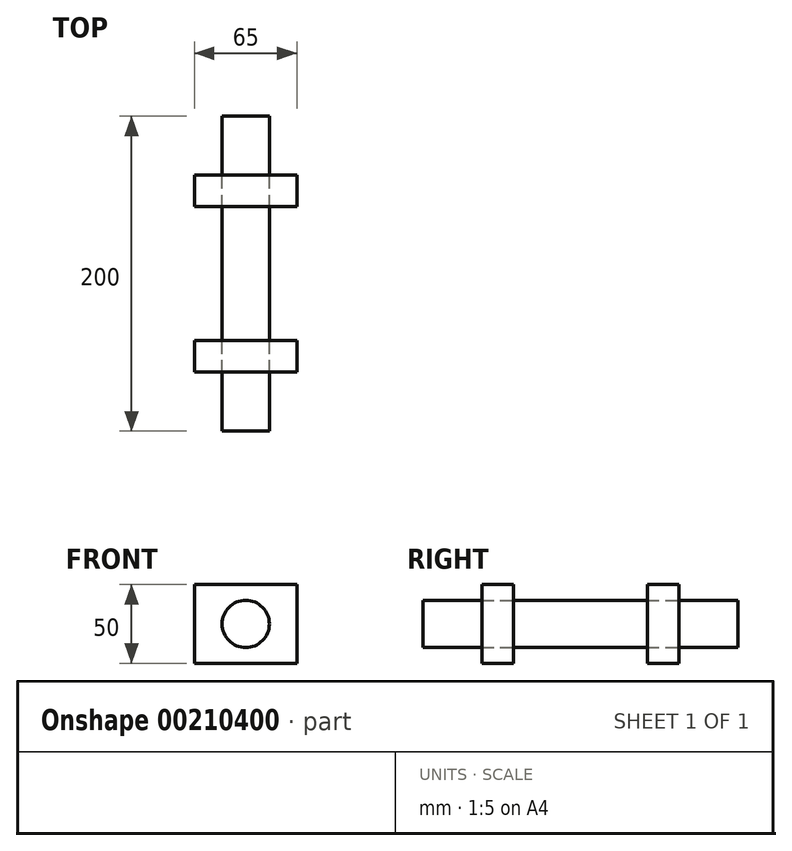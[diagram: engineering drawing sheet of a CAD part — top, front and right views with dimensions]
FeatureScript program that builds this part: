
annotation { "Feature Type Name" : "Feature", "Feature Type Description" : "" }
export const myFeature = defineFeature(function(context is Context, id is Id, definition is map)
    precondition{}
    {
        {
            var Q0;
            Q0=qCreatedBy(makeId("Front.planeOp"),FACE);
            var sketch = newSketch(context, id + "F0", { "sketchPlane" : qUnion([Q0])});
            skCircle(sketch, "E0", {"center": v(0, 0) * mm, "radius": 15 * mm});
            skSolve(sketch);
        }
        {
            var Q0;
            Q0=makeQuery(id+"F0.imprint","IMPRINT",FACE,{"disambiguationData":[TD([[makeQuery(id+"F0.imprint","IMPRINT",EDGE,{"derivedFrom":sQuery(id+"F0.wireOp",EDGE,"E0")}),1.0]])]});
            extrude(context, id + "F1", {"entities" : qUnion([Q0]), "endBound" : BoundingType.SYMMETRIC, "depth" : 200 * mm});
        }
        {
            var Q0;
            Q0=qCreatedBy(makeId("Top.planeOp"),FACE);
            var sketch = newSketch(context, id + "F2", { "sketchPlane" : qUnion([Q0])});
            skLineSegment(sketch, "E1.bottom", {"start": v(-32.5, 62.5) * mm, "end": v(32.5, 62.5) * mm});
            skLineSegment(sketch, "E1.top", {"start": v(-32.5, 42.5) * mm, "end": v(32.5, 42.5) * mm});
            skLineSegment(sketch, "E1.left", {"start": v(-32.5, 62.5) * mm, "end": v(-32.5, 42.5) * mm});
            skLineSegment(sketch, "E1.right", {"start": v(32.5, 62.5) * mm, "end": v(32.5, 42.5) * mm});
            skLineSegment(sketch, "E2", {"start": v(0, 100) * mm, "end": v(0, -100) * mm, "construction": true});
            skLineSegment(sketch, "E3", {"start": v(0, 0) * mm, "end": v(-59.9, 0) * mm, "construction": true});
            skLineSegment(sketch, "E4.MirrorCS", {"start": v(-32.5, -42.5) * mm, "end": v(32.5, -42.5) * mm});
            skLineSegment(sketch, "E5.MirrorCS", {"start": v(-32.5, -62.5) * mm, "end": v(-32.5, -42.5) * mm});
            skLineSegment(sketch, "E6.MirrorCS", {"start": v(-32.5, -62.5) * mm, "end": v(32.5, -62.5) * mm});
            skLineSegment(sketch, "E7.MirrorCS", {"start": v(32.5, -62.5) * mm, "end": v(32.5, -42.5) * mm});
            skSolve(sketch);
        }
        {
            var Q0;
            Q0=makeQuery(id+"F2.imprint","IMPRINT",FACE,{"disambiguationData":[TD([[makeQuery(id+"F2.imprint","IMPRINT",EDGE,{"derivedFrom":sQuery(id+"F2.wireOp",EDGE,"E1.bottom")}),-1.0]])]});
            var Q1;
            Q1=makeQuery(id+"F2.imprint","IMPRINT",FACE,{"disambiguationData":[TD([[makeQuery(id+"F2.imprint","IMPRINT",EDGE,{"derivedFrom":sQuery(id+"F2.wireOp",EDGE,"E4.MirrorCS")}),-1.0]])]});
            extrude(context, id + "F3", {"entities" : qUnion([Q0, Q1]), "depth" : 25 * mm, "hasSecondDirection" : true, "secondDirectionOppositeDirection" : true, "secondDirectionDepth" : 25 * mm});
        }
    });
